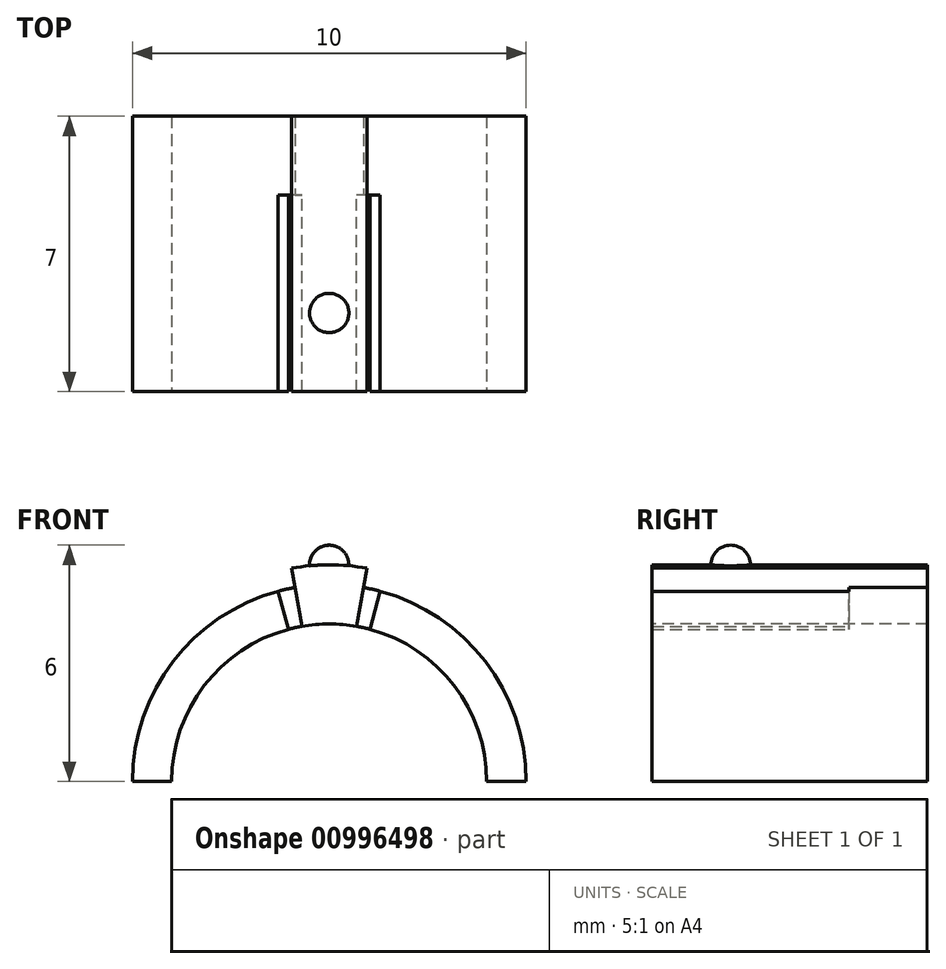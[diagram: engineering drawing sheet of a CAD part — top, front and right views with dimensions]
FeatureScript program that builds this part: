
annotation { "Feature Type Name" : "Feature", "Feature Type Description" : "" }
export const myFeature = defineFeature(function(context is Context, id is Id, definition is map)
    precondition{}
    {
        {
            var Q0;
            Q0=qCreatedBy(makeId("Front.planeOp"),FACE);
            var sketch = newSketch(context, id + "F0", { "sketchPlane" : qUnion([Q0])});
            skCircle(sketch, "E0", {"center": v(0, 0) * mm, "radius": 5 * mm});
            skCircle(sketch, "E1", {"center": v(0, 0) * mm, "radius": 4 * mm});
            skCircle(sketch, "E2", {"center": v(0, 0) * mm, "radius": 5.5 * mm});
            skLineSegment(sketch, "E3", {"start": v(-9.57, 0) * mm, "end": v(10.1, 0) * mm});
            skLineSegment(sketch, "E4", {"start": v(0, 0) * mm, "end": v(2.26, 8.43) * mm});
            skLineSegment(sketch, "E5", {"start": v(0, 0) * mm, "end": v(1.68, 9.54) * mm});
            skLineSegment(sketch, "E6.MirrorCS", {"start": v(0, 0) * mm, "end": v(-1.68, 9.54) * mm});
            skLineSegment(sketch, "E7.MirrorCS", {"start": v(0, 0) * mm, "end": v(-2.26, 8.43) * mm});
            skLineSegment(sketch, "E8", {"start": v(0, 0) * mm, "end": v(0, 8.45) * mm, "construction": true});
            skSolve(sketch);
        }
        {
            var Q0;
            {var subQ0=sQuery(id+"F0.wireOp",EDGE,"E4");var subQ1=sQuery(id+"F0.wireOp",EDGE,"E0");var subQ2=makeQuery(id+"F0.imprint","INTERSECT",VERTEX,{"derivedFrom":[subQ1,subQ0]});Q0=makeQuery(id+"F0.imprint","IMPRINT",FACE,{"disambiguationData":[TD([[makeQuery(id+"F0.imprint","IMPRINT",EDGE,{"disambiguationData":[TD([[subQ2,1.0]])],"derivedFrom":subQ1}),1.0]])]});}
            var Q1;
            {var subQ0=sQuery(id+"F0.wireOp",EDGE,"E4");var subQ1=sQuery(id+"F0.wireOp",EDGE,"E0");var subQ2=makeQuery(id+"F0.imprint","INTERSECT",VERTEX,{"derivedFrom":[subQ1,subQ0]});Q1=makeQuery(id+"F0.imprint","IMPRINT",FACE,{"disambiguationData":[TD([[makeQuery(id+"F0.imprint","IMPRINT",EDGE,{"disambiguationData":[TD([[subQ2,-1.0]])],"derivedFrom":subQ1}),1.0]])]});}
            var Q2;
            {var subQ0=sQuery(id+"F0.wireOp",EDGE,"E5");var subQ1=sQuery(id+"F0.wireOp",EDGE,"E0");var subQ2=makeQuery(id+"F0.imprint","INTERSECT",VERTEX,{"derivedFrom":[subQ1,subQ0]});Q2=makeQuery(id+"F0.imprint","IMPRINT",FACE,{"disambiguationData":[TD([[makeQuery(id+"F0.imprint","IMPRINT",EDGE,{"disambiguationData":[TD([[subQ2,-1.0]])],"derivedFrom":subQ1}),1.0]])]});}
            var Q3;
            {var subQ0=sQuery(id+"F0.wireOp",EDGE,"E6.MirrorCS");var subQ1=sQuery(id+"F0.wireOp",EDGE,"E0");var subQ2=makeQuery(id+"F0.imprint","INTERSECT",VERTEX,{"derivedFrom":[subQ1,subQ0]});Q3=makeQuery(id+"F0.imprint","IMPRINT",FACE,{"disambiguationData":[TD([[makeQuery(id+"F0.imprint","IMPRINT",EDGE,{"disambiguationData":[TD([[subQ2,-1.0]])],"derivedFrom":subQ1}),1.0]])]});}
            var Q4;
            {var subQ0=sQuery(id+"F0.wireOp",EDGE,"E7.MirrorCS");var subQ1=sQuery(id+"F0.wireOp",EDGE,"E0");var subQ2=makeQuery(id+"F0.imprint","INTERSECT",VERTEX,{"derivedFrom":[subQ1,subQ0]});Q4=makeQuery(id+"F0.imprint","IMPRINT",FACE,{"disambiguationData":[TD([[makeQuery(id+"F0.imprint","IMPRINT",EDGE,{"disambiguationData":[TD([[subQ2,-1.0]])],"derivedFrom":subQ1}),1.0]])]});}
            extrude(context, id + "F1", {"entities" : qUnion([Q0, Q1, Q2, Q3, Q4]), "oppositeDirection" : true, "depth" : 2 * mm, "offsetDistance" : 25 * mm});
        }
        {
            var Q0;
            {var subQ0=sQuery(id+"F0.wireOp",EDGE,"E5");var subQ1=sQuery(id+"F0.wireOp",EDGE,"E0");var subQ2=makeQuery(id+"F0.imprint","INTERSECT",VERTEX,{"derivedFrom":[subQ1,subQ0]});Q0=makeQuery(id+"F0.imprint","IMPRINT",FACE,{"disambiguationData":[TD([[makeQuery(id+"F0.imprint","IMPRINT",EDGE,{"disambiguationData":[TD([[subQ2,-1.0]])],"derivedFrom":subQ1}),1.0]])]});}
            var Q1;
            {var subQ0=sQuery(id+"F0.wireOp",EDGE,"E5");var subQ1=sQuery(id+"F0.wireOp",EDGE,"E0");var subQ2=makeQuery(id+"F0.imprint","INTERSECT",VERTEX,{"derivedFrom":[subQ1,subQ0]});Q1=makeQuery(id+"F0.imprint","IMPRINT",FACE,{"disambiguationData":[TD([[makeQuery(id+"F0.imprint","IMPRINT",EDGE,{"disambiguationData":[TD([[subQ2,-1.0]])],"derivedFrom":subQ1}),-1.0]])]});}
            extrude(context, id + "F2", {"entities" : qUnion([Q0, Q1]), "operationType" : NewBodyOperationType.ADD, "depth" : 5 * mm, "offsetDistance" : 25.4 * mm, "hasSecondDirection" : true, "secondDirectionOppositeDirection" : true, "secondDirectionDepth" : 2 * mm});
        }
        {
            var Q0;
            {var subQ0=sQuery(id+"F0.wireOp",EDGE,"E4");var subQ1=sQuery(id+"F0.wireOp",EDGE,"E0");var subQ2=makeQuery(id+"F0.imprint","INTERSECT",VERTEX,{"derivedFrom":[subQ1,subQ0]});Q0=makeQuery(id+"F0.imprint","IMPRINT",FACE,{"disambiguationData":[TD([[makeQuery(id+"F0.imprint","IMPRINT",EDGE,{"disambiguationData":[TD([[subQ2,1.0]])],"derivedFrom":subQ1}),1.0]])]});}
            var Q1;
            {var subQ0=sQuery(id+"F0.wireOp",EDGE,"E7.MirrorCS");var subQ1=sQuery(id+"F0.wireOp",EDGE,"E0");var subQ2=makeQuery(id+"F0.imprint","INTERSECT",VERTEX,{"derivedFrom":[subQ1,subQ0]});Q1=makeQuery(id+"F0.imprint","IMPRINT",FACE,{"disambiguationData":[TD([[makeQuery(id+"F0.imprint","IMPRINT",EDGE,{"disambiguationData":[TD([[subQ2,-1.0]])],"derivedFrom":subQ1}),1.0]])]});}
            extrude(context, id + "F3", {"entities" : qUnion([Q0, Q1]), "operationType" : NewBodyOperationType.ADD, "depth" : 5 * mm, "offsetDistance" : 25 * mm});
        }
        {
            var Q0;
            Q0=qCreatedBy(makeId("Front.planeOp"),FACE);
            cPlane(context, id + "F4", {"entities" : qUnion([Q0]), "cplaneType" : CPlaneType.OFFSET, "offset" : 3 * mm, "width" : 150 * mm, "height" : 150 * mm});
        }
        {
            var Q0;
            Q0=qCreatedBy(id+"F4.planeOp",FACE);
            var sketch = newSketch(context, id + "F5", { "sketchPlane" : qUnion([Q0])});
            skCircle(sketch, "E9.0", {"center": v(0, 0) * mm, "radius": 5.5 * mm, "construction": true});
            skLineSegment(sketch, "E9.1", {"start": v(0, 0) * mm, "end": v(0, 8.45) * mm});
            skCircle(sketch, "E10", {"center": v(0, 5.5) * mm, "radius": 0.5 * mm});
            skSolve(sketch);
        }
        {
            var Q0;
            {var subQ0=sQuery(id+"F5.wireOp",EDGE,"E10");var subQ1=sQuery(id+"F5.wireOp",EDGE,"E9.1");var subQ2=makeQuery(id+"F5.imprint","INTERSECT",VERTEX,{"disambiguationData":[OD(0.0)],"derivedFrom":[subQ1,subQ0]});Q0=makeQuery(id+"F5.imprint","IMPRINT",FACE,{"disambiguationData":[TD([[makeQuery(id+"F5.imprint","IMPRINT",EDGE,{"disambiguationData":[TD([[subQ2,-1.0]])],"derivedFrom":subQ1}),-1.0]])]});}
            var Q1;
            Q1=sQuery(id+"F5.wireOp",EDGE,"E9.1");
            revolve(context, id + "F6", {"operationType" : NewBodyOperationType.ADD, "surfaceOperationType" : NewSurfaceOperationType.NEW, "entities" : qUnion([Q0]), "axis" : qUnion([Q1]), "revolveType" : RevolveType.FULL});
        }
    });
